# Revit family: ШУВ-Ч_С300_Рубеж_ЮТ+ТЭН_18.03.25
name_source: partatom
category: Оборудование
units: mm (PartAtom-declared; Revit-internal decimal feet)

## family parameters
Всегда вертикально = Да
Классификация = Нет
На основе рабочей плоскости = Нет
Общий = Нет
При загрузке вырезать с полостями = Нет
Размер круглого соединителя = Использовать диаметр
Тип детали = Нормальный
Точка расчета площади = Нет

## types (4) — shared parameters
URL = https://plazma-t.ru
Группа модели = ШУВ-Ч+ТЭН
Изготовитель = ООО "Плазма-Т"
Назв гориз ПУШ = 210 мм
zero-valued in all types: Отметка по умолчанию

## per-type parameters (varying)
| type | A | B | Комментарии к типоразмеру | Расст ПУШ от верхней стенки | Расст ПУШ от левой стенки | Расст ввод от задней стенки | Расст ввод от левой стенки | Расст замок | Типоразмер шкафа | расст замок верт |
| ШУВ-Ч_С300_РЖ_ЮТ_0,37-15кВт + ТЭН 4-45кВт | 200 мм | 175 мм | Ш4/DEK | 110 мм | 335 мм | 60 мм | 410 мм | 55 мм | Ш4 | 400 мм |
| ШУВ-Ч_С300_РЖ_ЮТ_30-45кВт + ТЭН 4-45кВт | 250 мм | 225 мм | Ш6/DEK | 350 мм | 410 мм | 60 мм | 400 мм | 55 мм | Ш6 | 600 мм |
| ШУВ-Ч_С300_РЖ_ЮТ_55-90кВт + ТЭН 4-45кВт | 275 мм | 250 мм | Ш20/DEK | 380 мм | 308 мм | 150 мм | 400 мм | 70 мм | Ш20 | 1000 мм |
| ШУВ-Ч_С300_РЖ_ЮТ_18,5-22кВт + ТЭН 4-45кВт | 200 мм | 175 мм | Ш5/DEK | 160 мм | 360 мм | 60 мм | 375 мм | 55 мм | Ш5 | 450 мм |
